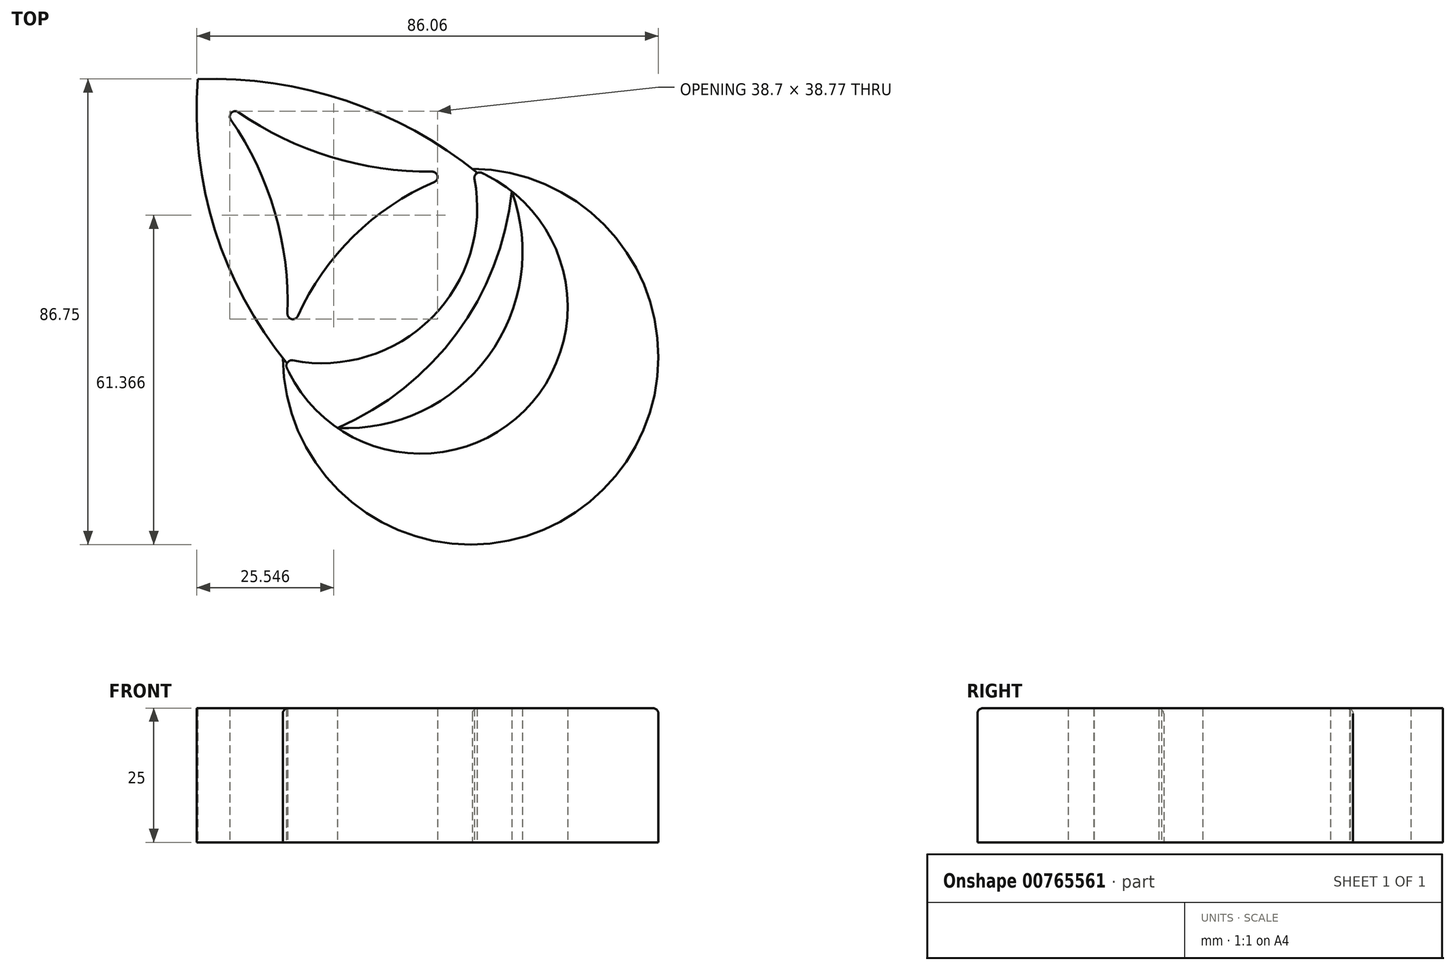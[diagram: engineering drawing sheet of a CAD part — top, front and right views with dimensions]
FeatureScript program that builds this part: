
annotation { "Feature Type Name" : "Feature", "Feature Type Description" : "" }
export const myFeature = defineFeature(function(context is Context, id is Id, definition is map)
    precondition{}
    {
        {
            var Q0;
            Q0=qCreatedBy(makeId("Top.planeOp"),FACE);
            var sketch = newSketch(context, id + "F0", { "sketchPlane" : qUnion([Q0])});
            skArc(sketch, "E0", {"start": v(-34.44, 8.03) * mm, "mid": v(21.42, -27.16) * mm, "end": v(0, 35.28) * mm});
            skPoint(sketch, "E1", {"position": v(-13, 31.83) * mm});
            skPoint(sketch, "E2", {"position": v(0, 35.28) * mm});
            skArc(sketch, "E3", {"start": v(-34.55, -1.82) * mm, "mid": v(9.75, -9.78) * mm, "end": v(1.82, 34.52) * mm});
            skArc(sketch, "E4", {"start": v(0, 35.28) * mm, "mid": v(-24.08, 48.18) * mm, "end": v(-51.13, 51.98) * mm});
            skArc(sketch, "E5", {"start": v(-51.13, 51.98) * mm, "mid": v(-48.14, 24.5) * mm, "end": v(-35.3, 0) * mm});
            skArc(sketch, "E6", {"start": v(-43.6, 45.86) * mm, "mid": v(-26.4, 37.51) * mm, "end": v(-7.46, 34.76) * mm});
            skArc(sketch, "E7", {"start": v(-34.43, 8.3) * mm, "mid": v(-36.8, 27.23) * mm, "end": v(-45, 44.47) * mm});
            skArc(sketch, "E8", {"start": v(-25.1, -13.02) * mm, "mid": v(2.97, 0.34) * mm, "end": v(7.4, 31.1) * mm});
            skArc(sketch, "E9", {"start": v(-25.1, -13.02) * mm, "mid": v(-2.88, 4.64) * mm, "end": v(7.4, 31.1) * mm});
            skArc(sketch, "E10", {"start": v(-33.45, -0.42) * mm, "mid": v(-7.55, 7.53) * mm, "end": v(0.42, 33.43) * mm});
            skArc(sketch, "E11", {"start": v(-35.3, 0) * mm, "mid": v(-11.94, 11.92) * mm, "end": v(0, 35.28) * mm});
            skArc(sketch, "E12", {"start": v(-7.06, 32.85) * mm, "mid": v(-22.12, 22.72) * mm, "end": v(-32.52, 7.84) * mm});
            skPoint(sketch, "E13.visualSharp", {"position": v(-51.13, 51.98) * mm});
            skArc(sketch, "E13.filletArc", {"start": v(-43.6, 45.86) * mm, "mid": v(-44.88, 45.74) * mm, "end": v(-45, 44.47) * mm});
            skArc(sketch, "E14.filletArc", {"start": v(-7.06, 32.85) * mm, "mid": v(-6.48, 33.97) * mm, "end": v(-7.46, 34.76) * mm});
            skPoint(sketch, "E15.visualSharp", {"position": v(-35.3, 0) * mm});
            skArc(sketch, "E15.filletArc", {"start": v(-34.43, 8.3) * mm, "mid": v(-33.65, 7.28) * mm, "end": v(-32.52, 7.84) * mm});
            skArc(sketch, "E16.filletArc", {"start": v(1.82, 34.52) * mm, "mid": v(0.78, 34.4) * mm, "end": v(0.42, 33.43) * mm});
            skArc(sketch, "E17.filletArc", {"start": v(-33.45, -0.42) * mm, "mid": v(-34.42, -0.78) * mm, "end": v(-34.55, -1.82) * mm});
            skSolve(sketch);
        }
        {
            var Q0;
            {var subQ3=sQuery(id+"F0.wireOp",EDGE,"E5");Q0=makeQuery(id+"F0.imprint","IMPRINT",FACE,{"disambiguationData":[TD([[makeQuery(id+"F0.imprint","IMPRINT",EDGE,{"derivedFrom":subQ3}),1.0]])]});}
            var Q1;
            {var subQ3=sQuery(id+"F0.wireOp",EDGE,"E3");var subQ7=sQuery(id+"F0.wireOp",EDGE,"E9");var subQ8=sQuery(id+"F0.wireOp",EDGE,"E8");var subQ9=makeQuery(id+"F0.imprint","INTERSECT",VERTEX,{"disambiguationData":[OD(0.0)],"derivedFrom":[subQ3,subQ8,subQ7]});Q1=makeQuery(id+"F0.imprint","IMPRINT",FACE,{"disambiguationData":[TD([[makeQuery(id+"F0.imprint","IMPRINT",EDGE,{"disambiguationData":[TD([[subQ9,-1.0]])],"derivedFrom":subQ3}),-1.0]])]});}
            var Q2;
            Q2=makeQuery(id+"F0.imprint","IMPRINT",FACE,{"disambiguationData":[TD([[makeQuery(id+"F0.imprint","IMPRINT",EDGE,{"derivedFrom":sQuery(id+"F0.wireOp",EDGE,"E8")}),1.0]])]});
            var Q3;
            Q3=makeQuery(id+"F0.imprint","IMPRINT",FACE,{"disambiguationData":[TD([[makeQuery(id+"F0.imprint","IMPRINT",EDGE,{"derivedFrom":sQuery(id+"F0.wireOp",EDGE,"E10")}),1.0]])]});
            var Q4;
            {var subQ1=sQuery(id+"F0.wireOp",EDGE,"E4");Q4=makeQuery(id+"F0.imprint","IMPRINT",FACE,{"disambiguationData":[TD([[makeQuery(id+"F0.imprint","IMPRINT",EDGE,{"derivedFrom":subQ1}),1.0]])]});}
            extrude(context, id + "F1", {"entities" : qUnion([Q0, Q1, Q2, Q3, Q4]), "depth" : 25 * mm, "offsetDistance" : 25 * mm});
        }
        {
            var Q0;
            Q0=makeQuery(id+"F1.opExtrude","CAP_EDGE",EDGE,{"disambiguationData":[OSD([sQuery(id+"F0.wireOp",EDGE,"E0")])],"isStart":false});
            fillet(context, id + "F2", {"entities" : qUnion([Q0]), "radius" : 1 * mm, "tangentPropagation" : true, "allowEdgeOverflow" : false});
        }
    });
